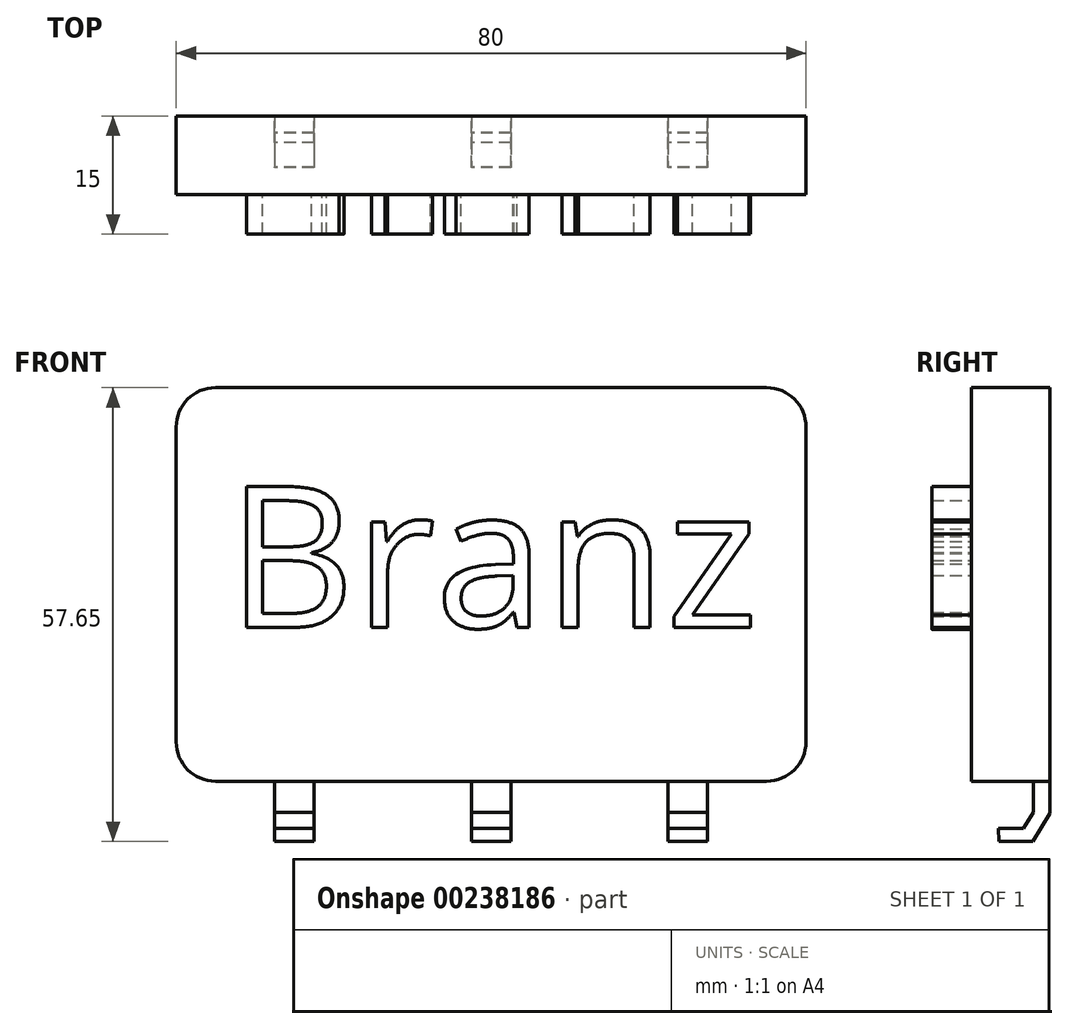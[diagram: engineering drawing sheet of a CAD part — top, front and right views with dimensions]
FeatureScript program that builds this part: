
annotation { "Feature Type Name" : "Feature", "Feature Type Description" : "" }
export const myFeature = defineFeature(function(context is Context, id is Id, definition is map)
    precondition{}
    {
        {
            var Q0;
            Q0=qCreatedBy(makeId("Front.planeOp"),FACE);
            var sketch = newSketch(context, id + "F0", { "sketchPlane" : qUnion([Q0])});
            skLineSegment(sketch, "E0.bottom", {"start": v(0, 0) * mm, "end": v(80, 0) * mm});
            skLineSegment(sketch, "E0.top", {"start": v(0, 50) * mm, "end": v(80, 50) * mm});
            skLineSegment(sketch, "E0.left", {"start": v(0, 0) * mm, "end": v(0, 50) * mm});
            skLineSegment(sketch, "E0.right", {"start": v(80, 0) * mm, "end": v(80, 50) * mm});
            skSolve(sketch);
        }
        {
            var Q0;
            Q0 = qSketchRegion(id + "F0", true);
            extrude(context, id + "F1", {"entities" : qUnion([Q0]), "depth" : 10 * mm});
        }
        {
            var Q0;
            Q0=makeQuery(id+"F1.opExtrude","CAP_FACE",FACE,{"disambiguationData":[OSD([sQuery(id+"F0.wireOp",EDGE,"E0.bottom"),sQuery(id+"F0.wireOp",EDGE,"E0.top"),sQuery(id+"F0.wireOp",EDGE,"E0.left"),sQuery(id+"F0.wireOp",EDGE,"E0.right")])],"isStart":false});
            var sketch = newSketch(context, id + "F2", { "sketchPlane" : qUnion([Q0])});
            skText(sketch, "E1", { "text": "Branz", "fontName": "OpenSans-Regular.ttf"});
            const initialGuessF2  = {"E1": [0.00645, 0.01955, 1, 0, 0.01804]};
            skSetInitialGuess(sketch, initialGuessF2);
            skSolve(sketch);
        }
        {
            var Q0;
            Q0 = qSketchRegion(id + "F2", true);
            extrude(context, id + "F3", {"entities" : qUnion([Q0]), "operationType" : NewBodyOperationType.ADD, "depth" : 5 * mm});
        }
        {
            var Q0;
            Q0=makeQuery(id+"F1.opExtrude","SWEPT_EDGE",EDGE,{"disambiguationData":[OSD([sQuery(id+"F0.wireOp",EDGE,"E0.top"),sQuery(id+"F0.wireOp",EDGE,"E0.left")])]});
            var Q1;
            Q1=makeQuery(id+"F1.opExtrude","SWEPT_EDGE",EDGE,{"disambiguationData":[OSD([sQuery(id+"F0.wireOp",EDGE,"E0.top"),sQuery(id+"F0.wireOp",EDGE,"E0.right")])]});
            var Q2;
            Q2=makeQuery(id+"F1.opExtrude","SWEPT_EDGE",EDGE,{"disambiguationData":[OSD([sQuery(id+"F0.wireOp",EDGE,"E0.bottom"),sQuery(id+"F0.wireOp",EDGE,"E0.right")])]});
            var Q3;
            Q3=makeQuery(id+"F1.opExtrude","SWEPT_EDGE",EDGE,{"disambiguationData":[OSD([sQuery(id+"F0.wireOp",EDGE,"E0.bottom"),sQuery(id+"F0.wireOp",EDGE,"E0.left")])]});
            fillet(context, id + "F4", {"entities" : qUnion([Q0, Q1, Q2, Q3]), "radius" : 5 * mm, "tangentPropagation" : true, "allowEdgeOverflow" : false});
        }
        {
            var Q0;
            Q0=qCreatedBy(makeId("Right.planeOp"),FACE);
            cPlane(context, id + "F5", {"entities" : qUnion([Q0]), "cplaneType" : CPlaneType.OFFSET, "offset" : 15 * mm, "width" : 150 * mm, "height" : 150 * mm});
        }
        {
            var Q0;
            Q0=qCreatedBy(id+"F5.planeOp",FACE);
            var sketch = newSketch(context, id + "F6", { "sketchPlane" : qUnion([Q0])});
            skLineSegment(sketch, "E2", {"start": v(0, 0) * mm, "end": v(0, -4.06) * mm});
            skLineSegment(sketch, "E3", {"start": v(0, -4.06) * mm, "end": v(-2.17, -7.65) * mm});
            skLineSegment(sketch, "E4", {"start": v(-2.17, -7.65) * mm, "end": v(-6.5, -7.65) * mm});
            skLineSegment(sketch, "E5", {"start": v(-3.4, -5.96) * mm, "end": v(-2.12, -3.99) * mm});
            skLineSegment(sketch, "E6", {"start": v(-2.12, -3.99) * mm, "end": v(-2.12, 0) * mm});
            skLineSegment(sketch, "E7", {"start": v(-2.12, 0) * mm, "end": v(0, 0) * mm});
            skLineSegment(sketch, "E8", {"start": v(-3.4, -5.96) * mm, "end": v(-6.53, -5.96) * mm});
            skLineSegment(sketch, "E9", {"start": v(-6.53, -5.96) * mm, "end": v(-6.5, -7.65) * mm});
            skSolve(sketch);
        }
        {
            var Q0;
            Q0 = qSketchRegion(id + "F6", true);
            extrude(context, id + "F7", {"entities" : qUnion([Q0]), "operationType" : NewBodyOperationType.ADD, "endBound" : BoundingType.SYMMETRIC, "depth" : 5 * mm});
        }
        {
            var Q0;
            Q0=qCreatedBy(id+"F5.planeOp",FACE);
            cPlane(context, id + "F8", {"entities" : qUnion([Q0]), "cplaneType" : CPlaneType.OFFSET, "offset" : 25 * mm, "width" : 150 * mm, "height" : 150 * mm});
        }
        {
            var Q0;
            Q0=qCreatedBy(id+"F8.planeOp",FACE);
            var sketch = newSketch(context, id + "F9", { "sketchPlane" : qUnion([Q0])});
            skLineSegment(sketch, "E10.0.4", {"start": v(-4.9, -5.96) * mm, "end": v(-4.9, -5.61) * mm});
            skLineSegment(sketch, "E11.0.0", {"start": v(-2.12, -3.99) * mm, "end": v(-3.4, -5.96) * mm});
            skLineSegment(sketch, "E11.0.1", {"start": v(-3.4, -5.96) * mm, "end": v(-6.53, -5.96) * mm});
            skLineSegment(sketch, "E11.0.2", {"start": v(-6.53, -5.96) * mm, "end": v(-6.5, -7.65) * mm});
            skLineSegment(sketch, "E11.0.3", {"start": v(-6.5, -7.65) * mm, "end": v(-2.17, -7.65) * mm});
            skLineSegment(sketch, "E11.0.4", {"start": v(-2.17, -7.65) * mm, "end": v(0, -4.06) * mm});
            skLineSegment(sketch, "E11.0.5", {"start": v(0, -4.06) * mm, "end": v(0, 0) * mm});
            skLineSegment(sketch, "E11.0.6", {"start": v(0, 0) * mm, "end": v(-2.12, 0) * mm});
            skLineSegment(sketch, "E11.0.7", {"start": v(-2.12, 0) * mm, "end": v(-2.12, -3.99) * mm});
            skSolve(sketch);
        }
        {
            var Q0;
            Q0=qCreatedBy(id+"F8.planeOp",FACE);
            cPlane(context, id + "F10", {"entities" : qUnion([Q0]), "cplaneType" : CPlaneType.OFFSET, "offset" : 25 * mm, "width" : 150 * mm, "height" : 150 * mm});
        }
        {
            var Q0;
            {var subQ3=sQuery(id+"F9.wireOp",EDGE,"E11.0.0");Q0=makeQuery(id+"F9.imprint","IMPRINT",FACE,{"disambiguationData":[TD([[makeQuery(id+"F9.imprint","IMPRINT",EDGE,{"derivedFrom":subQ3}),1.0]])]});}
            extrude(context, id + "F11", {"entities" : qUnion([Q0]), "operationType" : NewBodyOperationType.ADD, "endBound" : BoundingType.SYMMETRIC, "depth" : 5 * mm});
        }
        {
            var Q0;
            Q0=qCreatedBy(id+"F10.planeOp",FACE);
            var sketch = newSketch(context, id + "F12", { "sketchPlane" : qUnion([Q0])});
            skLineSegment(sketch, "E12.0.0", {"start": v(-2.12, -3.99) * mm, "end": v(-3.4, -5.96) * mm});
            skLineSegment(sketch, "E12.0.1", {"start": v(-3.4, -5.96) * mm, "end": v(-6.53, -5.96) * mm});
            skLineSegment(sketch, "E12.0.2", {"start": v(-6.53, -5.96) * mm, "end": v(-6.5, -7.65) * mm});
            skLineSegment(sketch, "E12.0.3", {"start": v(-6.5, -7.65) * mm, "end": v(-2.17, -7.65) * mm});
            skLineSegment(sketch, "E12.0.4", {"start": v(-2.17, -7.65) * mm, "end": v(0, -4.06) * mm});
            skLineSegment(sketch, "E12.0.5", {"start": v(0, -4.06) * mm, "end": v(0, 0) * mm});
            skLineSegment(sketch, "E12.0.6", {"start": v(0, 0) * mm, "end": v(-2.12, 0) * mm});
            skLineSegment(sketch, "E12.0.7", {"start": v(-2.12, 0) * mm, "end": v(-2.12, -3.99) * mm});
            skSolve(sketch);
        }
        {
            var Q0;
            Q0=makeQuery(id+"F12.imprint","IMPRINT",FACE,{"disambiguationData":[TD([[makeQuery(id+"F12.imprint","IMPRINT",EDGE,{"derivedFrom":sQuery(id+"F12.wireOp",EDGE,"E12.0.0")}),1.0]])]});
            extrude(context, id + "F13", {"entities" : qUnion([Q0]), "operationType" : NewBodyOperationType.ADD, "endBound" : BoundingType.SYMMETRIC, "depth" : 5 * mm});
        }
    });
